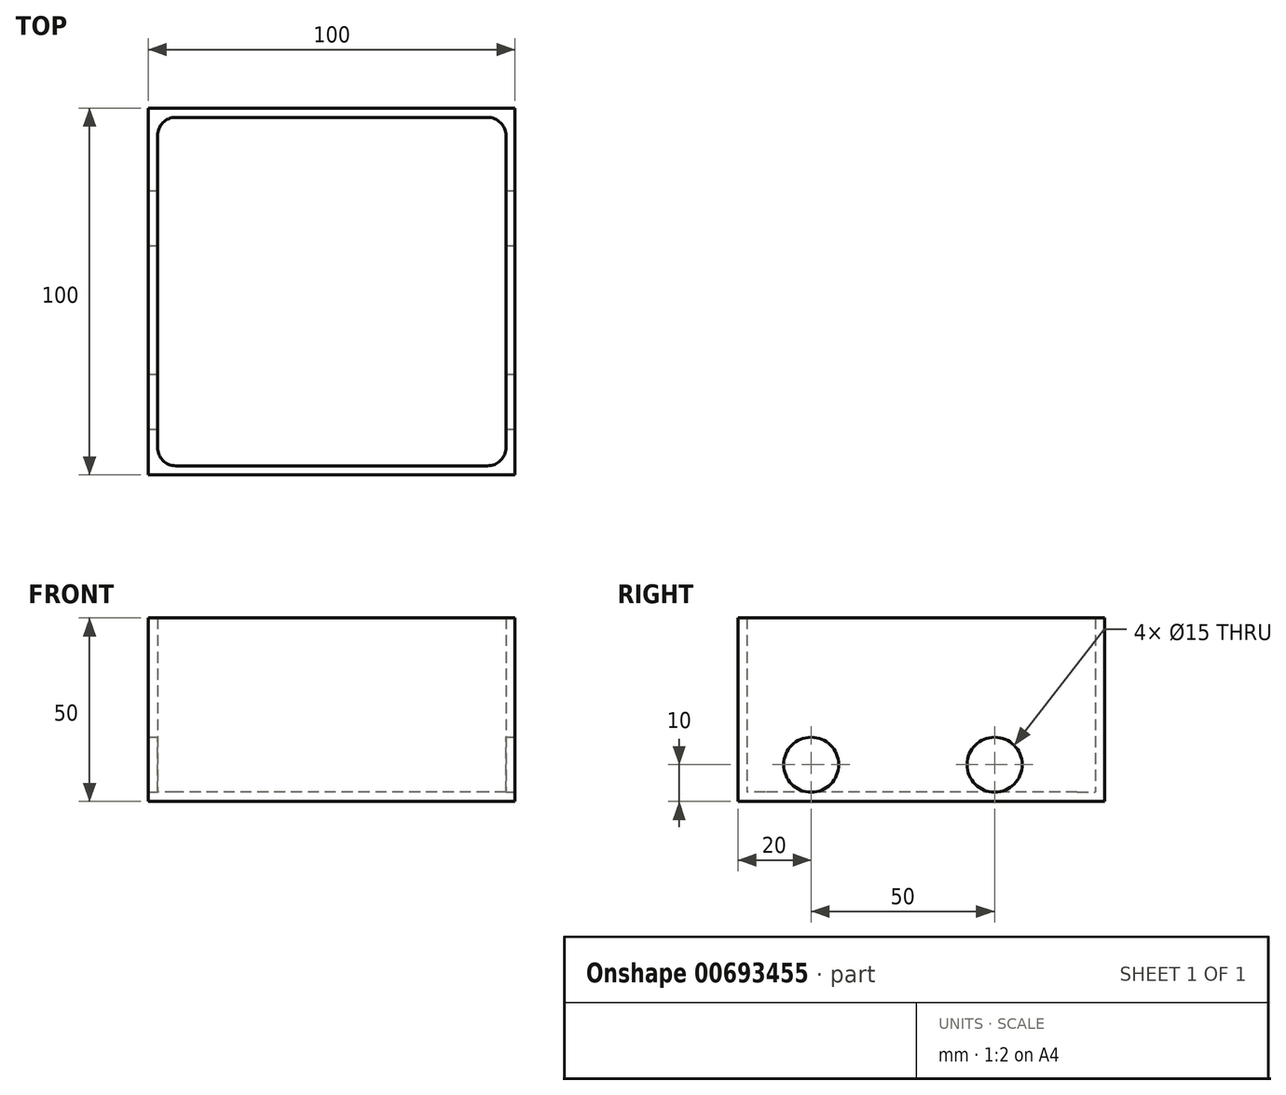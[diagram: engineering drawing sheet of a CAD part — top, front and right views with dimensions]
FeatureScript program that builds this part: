
annotation { "Feature Type Name" : "Feature", "Feature Type Description" : "" }
export const myFeature = defineFeature(function(context is Context, id is Id, definition is map)
    precondition{}
    {
        {
            var Q0;
            Q0=qCreatedBy(makeId("Top.planeOp"),FACE);
            var sketch = newSketch(context, id + "F0", { "sketchPlane" : qUnion([Q0])});
            skLineSegment(sketch, "E0.bottom", {"start": v(50, 50) * mm, "end": v(-50, 50) * mm});
            skLineSegment(sketch, "E0.top", {"start": v(50, -50) * mm, "end": v(-50, -50) * mm});
            skLineSegment(sketch, "E0.left", {"start": v(50, 50) * mm, "end": v(50, -50) * mm});
            skLineSegment(sketch, "E0.right", {"start": v(-50, 50) * mm, "end": v(-50, -50) * mm});
            skPoint(sketch, "E0.middle", {"position": v(0, 0) * mm});
            skSolve(sketch);
        }
        {
            var Q0;
            Q0 = qSketchRegion(id + "F0", true);
            extrude(context, id + "F1", {"entities" : qUnion([Q0]), "depth" : 50 * mm, "offsetDistance" : 25 * mm});
        }
        {
            var Q0;
            Q0=makeQuery(id+"F1.opExtrude","CAP_FACE",FACE,{"disambiguationData":[OSD([sQuery(id+"F0.wireOp",EDGE,"E0.bottom"),sQuery(id+"F0.wireOp",EDGE,"E0.top"),sQuery(id+"F0.wireOp",EDGE,"E0.left"),sQuery(id+"F0.wireOp",EDGE,"E0.right")])],"isStart":false});
            shell(context, id + "F2", {"entities" : qUnion([Q0]), "thickness" : 2.5 * mm});
        }
        {
            var Q0;
            Q0=makeQuery(id+"F2.opShell","OFFSET_EDGE",EDGE,{"disambiguationData":[OSD([sQuery(id+"F0.wireOp",EDGE,"E0.bottom"),sQuery(id+"F0.wireOp",EDGE,"E0.right")])]});
            var Q1;
            Q1=makeQuery(id+"F2.opShell","OFFSET_EDGE",EDGE,{"disambiguationData":[OSD([sQuery(id+"F0.wireOp",EDGE,"E0.bottom"),sQuery(id+"F0.wireOp",EDGE,"E0.left")])]});
            var Q2;
            Q2=makeQuery(id+"F2.opShell","OFFSET_EDGE",EDGE,{"disambiguationData":[OSD([sQuery(id+"F0.wireOp",EDGE,"E0.top"),sQuery(id+"F0.wireOp",EDGE,"E0.right")])]});
            var Q3;
            Q3=makeQuery(id+"F2.opShell","OFFSET_EDGE",EDGE,{"disambiguationData":[OSD([sQuery(id+"F0.wireOp",EDGE,"E0.top"),sQuery(id+"F0.wireOp",EDGE,"E0.left")])]});
            fillet(context, id + "F3", {"entities" : qUnion([Q0, Q1, Q2, Q3]), "radius" : 5 * mm, "tangentPropagation" : true, "allowEdgeOverflow" : false});
        }
        {
            var Q0;
            Q0=makeQuery(id+"F1.opExtrude","SWEPT_FACE",FACE,{"disambiguationData":[OSD([sQuery(id+"F0.wireOp",EDGE,"E0.left")])]});
            var sketch = newSketch(context, id + "F4", { "sketchPlane" : qUnion([Q0])});
            skCircle(sketch, "E1", {"center": v(-30, 10) * mm, "radius": 7.5 * mm});
            skCircle(sketch, "E2", {"center": v(20, 10) * mm, "radius": 7.5 * mm});
            skSolve(sketch);
        }
        {
            var Q0;
            Q0 = qSketchRegion(id + "F4", true);
            extrude(context, id + "F5", {"entities" : qUnion([Q0]), "operationType" : NewBodyOperationType.REMOVE, "endBound" : BoundingType.THROUGH_ALL, "oppositeDirection" : true, "depth" : 25 * mm, "offsetDistance" : 25 * mm});
        }
    });
